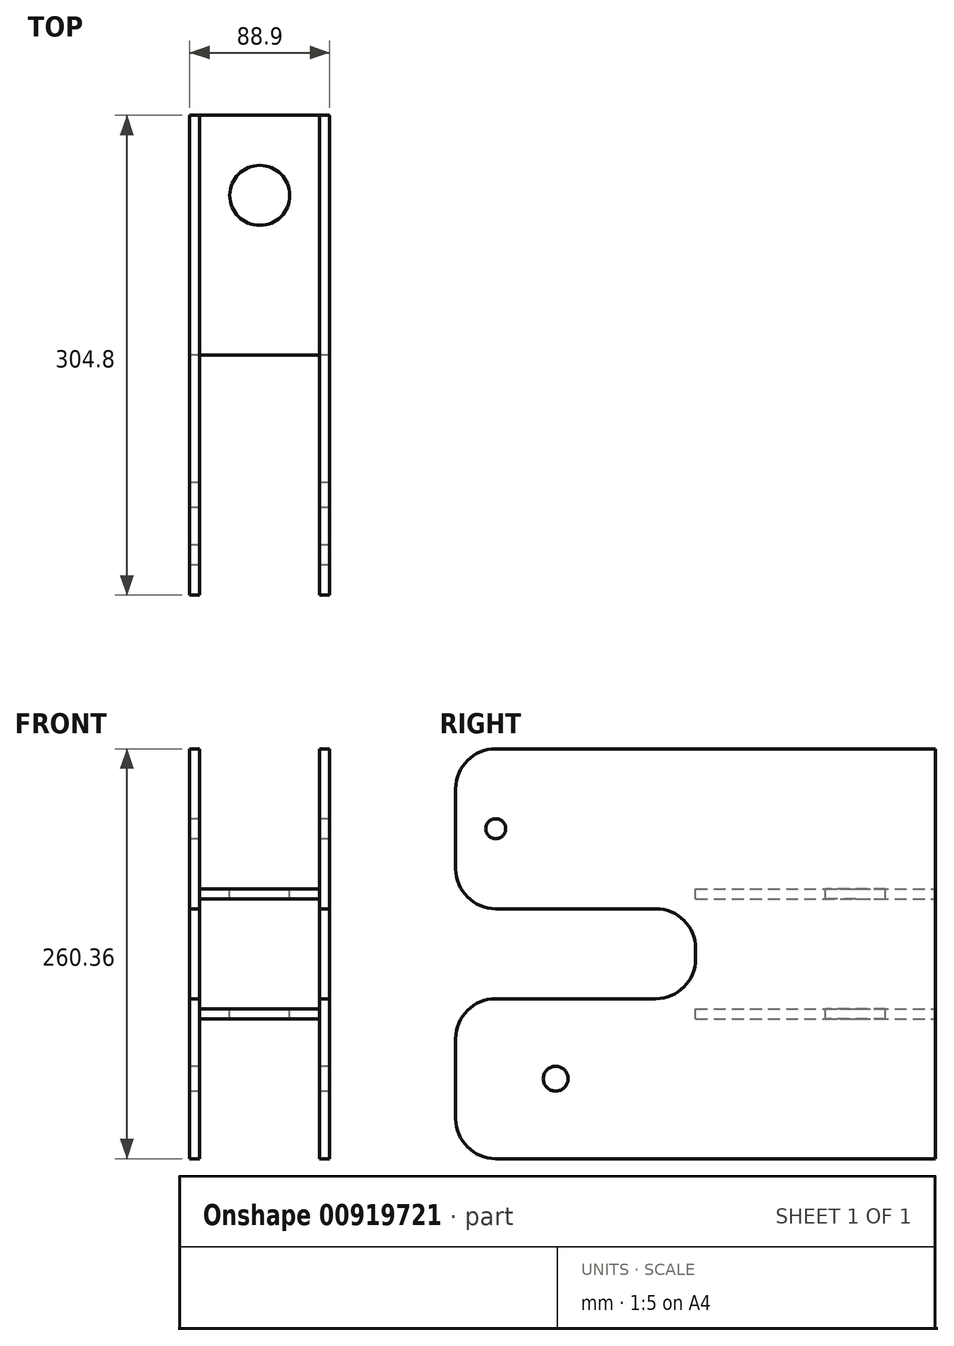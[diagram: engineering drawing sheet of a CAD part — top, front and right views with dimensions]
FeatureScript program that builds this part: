
annotation { "Feature Type Name" : "Feature", "Feature Type Description" : "" }
export const myFeature = defineFeature(function(context is Context, id is Id, definition is map)
    precondition{}
    {
        {
            var Q0;
            Q0=qCreatedBy(makeId("Right.planeOp"),FACE);
            var sketch = newSketch(context, id + "F0", { "sketchPlane" : qUnion([Q0])});
            skLineSegment(sketch, "E0.bottom", {"start": v(-127, 130.18) * mm, "end": v(152.4, 130.18) * mm});
            skLineSegment(sketch, "E0.top", {"start": v(-127, -130.18) * mm, "end": v(152.4, -130.18) * mm});
            skLineSegment(sketch, "E0.left", {"start": v(-152.4, 104.78) * mm, "end": v(-152.4, 53.98) * mm});
            skLineSegment(sketch, "E0.right", {"start": v(152.4, 130.18) * mm, "end": v(152.4, -130.18) * mm});
            skPoint(sketch, "E0.middle", {"position": v(0, 0) * mm});
            skLineSegment(sketch, "E1", {"start": v(-127, 28.58) * mm, "end": v(-25.4, 28.58) * mm});
            skLineSegment(sketch, "E2", {"start": v(0, 3.18) * mm, "end": v(0, -3.18) * mm});
            skLineSegment(sketch, "E3", {"start": v(-25.4, -28.58) * mm, "end": v(-127, -28.57) * mm});
            skLineSegment(sketch, "E4.trimOffspring", {"start": v(-152.4, -53.97) * mm, "end": v(-152.4, -104.78) * mm});
            skPoint(sketch, "E5.visualSharp", {"position": v(-152.4, 130.18) * mm});
            skArc(sketch, "E5.filletArc", {"start": v(-127, 130.18) * mm, "mid": v(-144.96, 122.74) * mm, "end": v(-152.4, 104.78) * mm});
            skPoint(sketch, "E6.visualSharp", {"position": v(152.4, 130.18) * mm});
            skPoint(sketch, "E7.visualSharp", {"position": v(152.4, -130.18) * mm});
            skPoint(sketch, "E8.visualSharp", {"position": v(-152.4, -28.57) * mm});
            skArc(sketch, "E8.filletArc", {"start": v(-127, -28.57) * mm, "mid": v(-144.96, -36.01) * mm, "end": v(-152.4, -53.98) * mm});
            skPoint(sketch, "E9.visualSharp", {"position": v(-152.4, 28.58) * mm});
            skArc(sketch, "E9.filletArc", {"start": v(-152.4, 53.98) * mm, "mid": v(-144.96, 36.01) * mm, "end": v(-127, 28.57) * mm});
            skPoint(sketch, "E10.visualSharp", {"position": v(0, -28.58) * mm});
            skArc(sketch, "E10.filletArc", {"start": v(-25.4, -28.57) * mm, "mid": v(-7.44, -21.14) * mm, "end": v(0, -3.18) * mm});
            skPoint(sketch, "E11.visualSharp", {"position": v(0, 28.58) * mm});
            skArc(sketch, "E11.filletArc", {"start": v(0, 3.18) * mm, "mid": v(-7.44, 21.14) * mm, "end": v(-25.4, 28.57) * mm});
            skPoint(sketch, "E12.visualSharp", {"position": v(-152.4, -130.18) * mm});
            skArc(sketch, "E12.filletArc", {"start": v(-152.4, -104.78) * mm, "mid": v(-144.96, -122.74) * mm, "end": v(-127, -130.18) * mm});
            skCircle(sketch, "E13", {"center": v(-127, 79.38) * mm, "radius": 6.35 * mm});
            skCircle(sketch, "E14", {"center": v(-88.9, -79.38) * mm, "radius": 7.94 * mm});
            skSolve(sketch);
        }
        {
            var Q0;
            Q0 = qSketchRegion(id + "F0", true);
            extrude(context, id + "F1", {"entities" : qUnion([Q0]), "endBound" : BoundingType.SYMMETRIC, "depth" : 88.9 * mm, "offsetDistance" : 25.4 * mm});
        }
        {
            var Q0;
            Q0=makeQuery(id+"F1.opExtrude","SWEPT_FACE",FACE,{"disambiguationData":[OSD([sQuery(id+"F0.wireOp",EDGE,"E0.right")])]});
            var sketch = newSketch(context, id + "F2", { "sketchPlane" : qUnion([Q0])});
            skLineSegment(sketch, "E15.bottom", {"start": v(-38.1, 130.18) * mm, "end": v(38.1, 130.18) * mm});
            skLineSegment(sketch, "E15.top", {"start": v(-38.1, 41.28) * mm, "end": v(38.1, 41.28) * mm});
            skLineSegment(sketch, "E15.left", {"start": v(-38.1, 130.18) * mm, "end": v(-38.1, 41.28) * mm});
            skLineSegment(sketch, "E15.right", {"start": v(38.1, 130.18) * mm, "end": v(38.1, 41.28) * mm});
            skLineSegment(sketch, "E16.MirrorCS", {"start": v(-38.1, -130.17) * mm, "end": v(-38.1, -41.27) * mm});
            skLineSegment(sketch, "E17.MirrorCS", {"start": v(38.1, -130.17) * mm, "end": v(38.1, -41.27) * mm});
            skLineSegment(sketch, "E18.MirrorCS", {"start": v(-38.1, -41.27) * mm, "end": v(38.1, -41.27) * mm});
            skLineSegment(sketch, "E19.bottom", {"start": v(-38.1, 34.93) * mm, "end": v(38.1, 34.93) * mm});
            skLineSegment(sketch, "E19.top", {"start": v(-38.1, -34.92) * mm, "end": v(38.1, -34.92) * mm});
            skLineSegment(sketch, "E19.left", {"start": v(-38.1, 34.93) * mm, "end": v(-38.1, -34.92) * mm});
            skLineSegment(sketch, "E19.right", {"start": v(38.1, 34.93) * mm, "end": v(38.1, -34.92) * mm});
            skSolve(sketch);
        }
        {
            var Q0;
            Q0=makeQuery(id+"F2.imprint","IMPRINT",FACE,{"disambiguationData":[TD([[makeQuery(id+"F2.imprint","IMPRINT",EDGE,{"derivedFrom":sQuery(id+"F2.wireOp",EDGE,"E15.bottom")}),-1.0]])]});
            var Q1;
            Q1=makeQuery(id+"F2.imprint","IMPRINT",FACE,{"disambiguationData":[TD([[makeQuery(id+"F2.imprint","IMPRINT",EDGE,{"derivedFrom":sQuery(id+"F2.wireOp",EDGE,"E19.bottom")}),-1.0]])]});
            var Q2;
            {var subQ0=sQuery(id+"F2.wireOp",EDGE,"E16.MirrorCS");Q2=makeQuery(id+"F2.imprint","IMPRINT",FACE,{"disambiguationData":[TD([[makeQuery(id+"F2.imprint","IMPRINT",EDGE,{"derivedFrom":subQ0}),-1.0]])]});}
            extrude(context, id + "F3", {"entities" : qUnion([Q0, Q1, Q2]), "operationType" : NewBodyOperationType.REMOVE, "endBound" : BoundingType.THROUGH_ALL, "oppositeDirection" : true, "depth" : 25.4 * mm, "offsetDistance" : 25.4 * mm});
        }
        {
            var Q0;
            Q0=makeQuery(id+"F3.boolean.opBoolean","COPY",FACE,{"derivedFrom":makeQuery(id+"F3.opExtrude","SWEPT_FACE",FACE,{"disambiguationData":[OSD([sQuery(id+"F2.wireOp",EDGE,"E15.top")])]})});
            var sketch = newSketch(context, id + "F4", { "sketchPlane" : qUnion([Q0])});
            skLineSegment(sketch, "E20", {"start": v(38.1, 0) * mm, "end": v(-38.1, 0) * mm});
            skPoint(sketch, "E20.startSnap0", {"position": v(38.1, 1.7) * mm});
            skCircle(sketch, "E21", {"center": v(0, 101.6) * mm, "radius": 19.05 * mm});
            skSolve(sketch);
        }
        {
            var Q0;
            {var subQ0=sQuery(id+"F4.wireOp",EDGE,"E20");Q0=makeQuery(id+"F4.imprint","IMPRINT",FACE,{"disambiguationData":[TD([[makeQuery(id+"F4.imprint","IMPRINT",EDGE,{"derivedFrom":subQ0}),1.0]])]});}
            var Q1;
            Q1=makeQuery(id+"F4.imprint","IMPRINT",FACE,{"disambiguationData":[TD([[makeQuery(id+"F4.imprint","IMPRINT",EDGE,{"derivedFrom":sQuery(id+"F4.wireOp",EDGE,"E21")}),1.0]])]});
            extrude(context, id + "F5", {"entities" : qUnion([Q0, Q1]), "operationType" : NewBodyOperationType.REMOVE, "endBound" : BoundingType.THROUGH_ALL, "oppositeDirection" : true, "depth" : 25.4 * mm, "offsetDistance" : 25.4 * mm});
        }
    });
